# Revit family: Access_Door-Acudor-Universal_Flush-BP-2002_Series
name_source: partatom
category: Specialty Equipment
revit_build: Autodesk Revit 2014 (Build: 20130308_1515(x64)
units: mm (PartAtom-declared; Revit-internal decimal feet)

## types (5) — shared parameters
Allen Head Cam Latch = No
Assembly Code = C1020700
Ceiling-Mounted = Yes
Cylinder Lock = Yes
Default Elevation = 48"
Description = Beveled Universal Flush
Finish = Stainless Steel-Acudor-16 Gauge-Alkyd White Enamel
Installation Type = Ceiling-Mounted
Length = 1 5/8"
Manufacturer = Acudor
Material = Stainless Steel-Acudor-16 Gauge-Alkyd White Enamel
Product Documentation Link = https://www.acudor.com
Product Page URL = https://www.acudor.com
Screwdriver Operated Cam Latch = Yes
Spanner Head Cam Latch = No
URL = http://acudor.com
Wall Mounted = No

## per-type parameters (varying)
| type | Height | Width |
| BP-2002 8x8 | 8" | 8" |
| BP-2002 12x12 | 12" | 12" |
| BP-2002 16x16 | 16" | 16" |
| BP-2002 18x18 | 18" | 18" |
| BP-2002 24x24 | 24" | 24" |

note: column(s) folded — value = type name in every type: Model

## geometry (parser evidence)
native form markers: Sweep x1
no freeform markers — native parametric forms only
